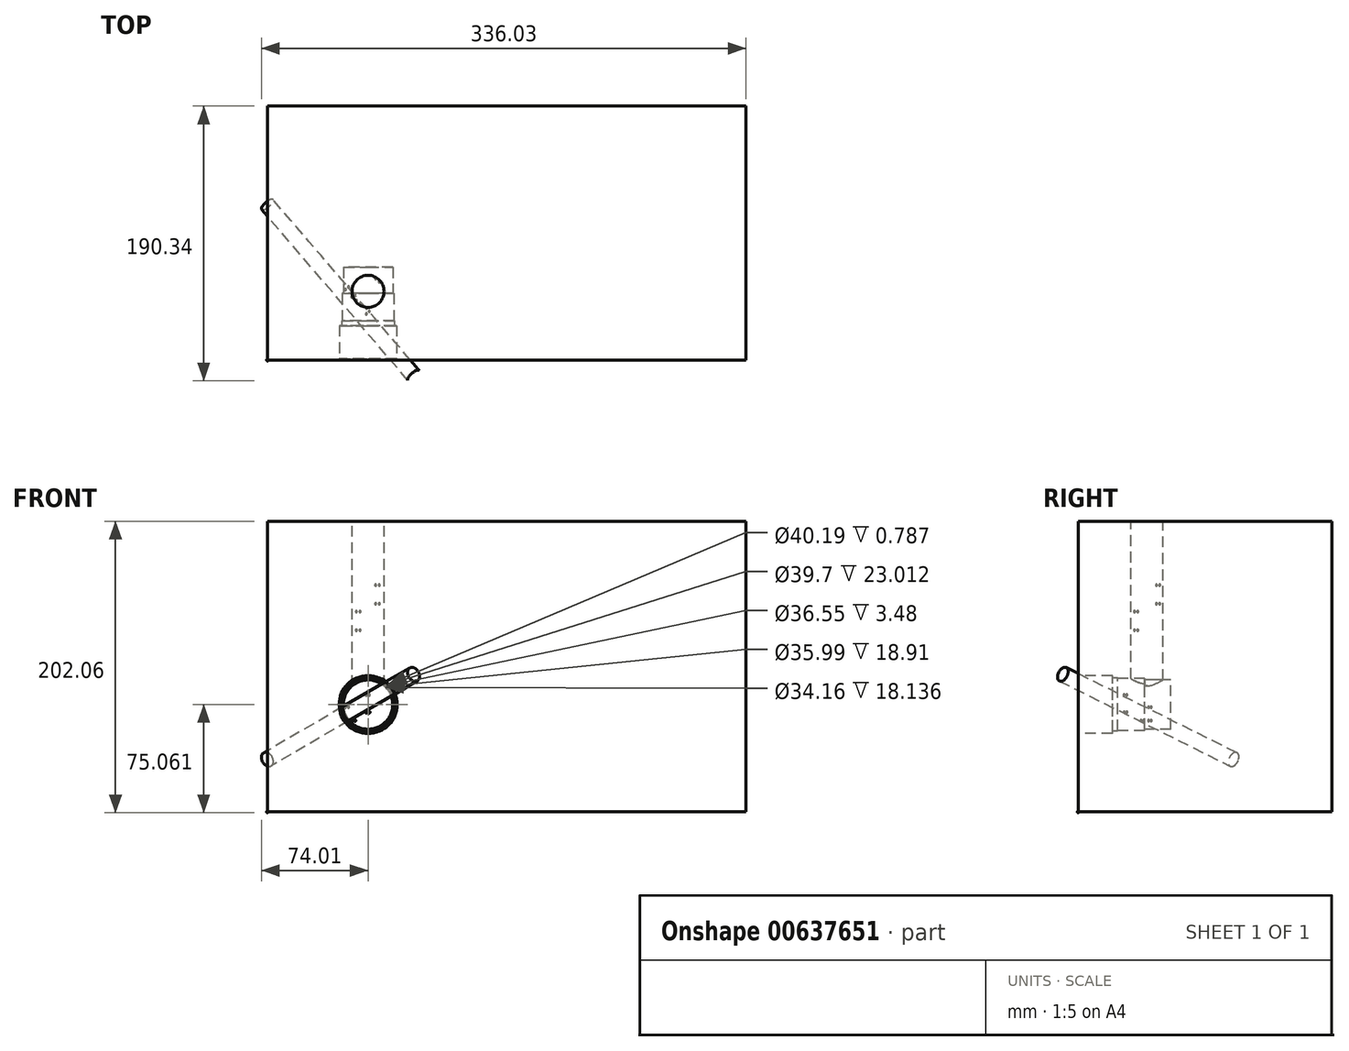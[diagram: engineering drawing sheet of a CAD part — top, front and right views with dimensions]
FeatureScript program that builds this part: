
annotation { "Feature Type Name" : "Feature", "Feature Type Description" : "" }
export const myFeature = defineFeature(function(context is Context, id is Id, definition is map)
    precondition{}
    {
        {
            var Q0;
            Q0=qCreatedBy(makeId("Top.planeOp"),FACE);
            var sketch = newSketch(context, id + "F0", { "sketchPlane" : qUnion([Q0])});
            skLineSegment(sketch, "E0.bottom", {"start": v(0, 0) * mm, "end": v(331.87, 0) * mm});
            skLineSegment(sketch, "E0.top", {"start": v(0, 176.02) * mm, "end": v(331.87, 176.02) * mm});
            skLineSegment(sketch, "E0.left", {"start": v(0, 0) * mm, "end": v(0, 176.02) * mm});
            skLineSegment(sketch, "E0.right", {"start": v(331.87, 0) * mm, "end": v(331.87, 176.02) * mm});
            skSolve(sketch);
        }
        {
            var Q0;
            Q0 = qSketchRegion(id + "F0", true);
            var Q1;
            Q1=sQuery(id+"F0.wireOp",EDGE,"E0.left");
            var Q2;
            Q2=sQuery(id+"F0.wireOp",EDGE,"E0.bottom");
            var Q3;
            Q3=sQuery(id+"F0.wireOp",EDGE,"E0.top");
            var Q4;
            Q4=sQuery(id+"F0.wireOp",EDGE,"E0.right");
            extrude(context, id + "F1", {"entities" : qUnion([Q0]), "surfaceEntities" : qUnion([Q1, Q2, Q3, Q4]), "depth" : 201.42 * mm, "offsetDistance" : 25.4 * mm});
        }
        {
            var Q0;
            Q0=qCreatedBy(makeId("Front.planeOp"),FACE);
            var sketch = newSketch(context, id + "F2", { "sketchPlane" : qUnion([Q0])});
            skArc(sketch, "E1", {"start": v(0, -0.64) * mm, "mid": v(0.64, 0) * mm, "end": v(0, 0.64) * mm});
            skLineSegment(sketch, "E2", {"start": v(0, 0.64) * mm, "end": v(0, -0.64) * mm});
            skSolve(sketch);
        }
        {
            var Q0;
            Q0=makeQuery(id+"F2.imprint","IMPRINT",FACE,{"disambiguationData":[TD([[makeQuery(id+"F2.imprint","IMPRINT",EDGE,{"derivedFrom":sQuery(id+"F2.wireOp",EDGE,"E1")}),1.0]])]});
            var Q1;
            Q1=sQuery(id+"F2.wireOp",EDGE,"E1");
            var Q2;
            Q2=sQuery(id+"F2.wireOp",EDGE,"E2");
            revolve(context, id + "F3", {"entities" : qUnion([Q0]), "surfaceEntities" : qUnion([Q1]), "axis" : qUnion([Q2]), "revolveType" : RevolveType.FULL});
        }
        {
            var Q0;
            Q0=makeQuery(id+"F3.opRevolve","SWEPT_BODY",BODY,{"disambiguationData":[OSD([sQuery(id+"F2.wireOp",EDGE,"E1"),sQuery(id+"F2.wireOp",EDGE,"E2")])]});
            transform(context, id + "F4", {"entities" : qUnion([Q0]), "transformType" : TransformType.TRANSLATION_3D, "dx" : 77.65 * mm, "dy" : 54.25 * mm, "dz" : 157.2 * mm, "makeCopy" : true});
        }
        {
            var Q0;
            Q0=makeQuery(id+"F3.opRevolve","SWEPT_BODY",BODY,{"disambiguationData":[OSD([sQuery(id+"F2.wireOp",EDGE,"E1"),sQuery(id+"F2.wireOp",EDGE,"E2")])]});
            transform(context, id + "F5", {"entities" : qUnion([Q0]), "transformType" : TransformType.TRANSLATION_3D, "dx" : 64.3 * mm, "dy" : 39.03 * mm, "dz" : 125.97 * mm, "makeCopy" : true});
        }
        {
            var Q0;
            Q0=makeQuery(id+"F3.opRevolve","SWEPT_BODY",BODY,{"disambiguationData":[OSD([sQuery(id+"F2.wireOp",EDGE,"E1"),sQuery(id+"F2.wireOp",EDGE,"E2")])]});
            transform(context, id + "F6", {"entities" : qUnion([Q0]), "transformType" : TransformType.TRANSLATION_3D, "dx" : 77.65 * mm, "dy" : 54.25 * mm, "dz" : 144.3 * mm, "makeCopy" : true});
        }
        {
            var Q0;
            Q0=makeQuery(id+"F3.opRevolve","SWEPT_BODY",BODY,{"disambiguationData":[OSD([sQuery(id+"F2.wireOp",EDGE,"E1"),sQuery(id+"F2.wireOp",EDGE,"E2")])]});
            transform(context, id + "F7", {"entities" : qUnion([Q0]), "transformType" : TransformType.TRANSLATION_3D, "dx" : 64.3 * mm, "dy" : 39.03 * mm, "dz" : 138.86 * mm, "makeCopy" : true});
        }
        {
            var Q0;
            Q0=makeQuery(id+"F3.opRevolve","SWEPT_BODY",BODY,{"disambiguationData":[OSD([sQuery(id+"F2.wireOp",EDGE,"E1"),sQuery(id+"F2.wireOp",EDGE,"E2")])]});
            transform(context, id + "F8", {"entities" : qUnion([Q0]), "transformType" : TransformType.TRANSLATION_3D, "dx" : 75.06 * mm, "dy" : 56.52 * mm, "dz" : 157.2 * mm, "makeCopy" : true});
        }
        {
            var Q0;
            Q0=makeQuery(id+"F3.opRevolve","SWEPT_BODY",BODY,{"disambiguationData":[OSD([sQuery(id+"F2.wireOp",EDGE,"E1"),sQuery(id+"F2.wireOp",EDGE,"E2")])]});
            transform(context, id + "F9", {"entities" : qUnion([Q0]), "transformType" : TransformType.TRANSLATION_3D, "dx" : 61.7 * mm, "dy" : 41.3 * mm, "dz" : 125.97 * mm, "makeCopy" : true});
        }
        {
            var Q0;
            Q0=makeQuery(id+"F3.opRevolve","SWEPT_BODY",BODY,{"disambiguationData":[OSD([sQuery(id+"F2.wireOp",EDGE,"E1"),sQuery(id+"F2.wireOp",EDGE,"E2")])]});
            transform(context, id + "F10", {"entities" : qUnion([Q0]), "transformType" : TransformType.TRANSLATION_3D, "dx" : 75.06 * mm, "dy" : 56.52 * mm, "dz" : 144.3 * mm, "makeCopy" : true});
        }
        {
            var Q0;
            Q0=makeQuery(id+"F3.opRevolve","SWEPT_BODY",BODY,{"disambiguationData":[OSD([sQuery(id+"F2.wireOp",EDGE,"E1"),sQuery(id+"F2.wireOp",EDGE,"E2")])]});
            transform(context, id + "F11", {"entities" : qUnion([Q0]), "transformType" : TransformType.TRANSLATION_3D, "dx" : 61.7 * mm, "dy" : 41.3 * mm, "dz" : 138.86 * mm, "makeCopy" : true});
        }
        {
            var Q0;
            Q0=makeQuery(id+"F1.opExtrude","CAP_FACE",FACE,{"disambiguationData":[OSD([sQuery(id+"F0.wireOp",EDGE,"E0.bottom"),sQuery(id+"F0.wireOp",EDGE,"E0.top"),sQuery(id+"F0.wireOp",EDGE,"E0.left"),sQuery(id+"F0.wireOp",EDGE,"E0.right")])],"isStart":false});
            var sketch = newSketch(context, id + "F12", { "sketchPlane" : qUnion([Q0])});
            skCircle(sketch, "E3", {"center": v(69.85, 47.62) * mm, "radius": 11.11 * mm});
            skSolve(sketch);
        }
        {
            var Q0;
            Q0 = qSketchRegion(id + "F12", true);
            var Q1;
            Q1=makeQuery(id+"F1.opExtrude","CAP_FACE",FACE,{"disambiguationData":[OSD([sQuery(id+"F0.wireOp",EDGE,"E0.bottom"),sQuery(id+"F0.wireOp",EDGE,"E0.top"),sQuery(id+"F0.wireOp",EDGE,"E0.left"),sQuery(id+"F0.wireOp",EDGE,"E0.right")])],"isStart":false});
            extrude(context, id + "F13", {"entities" : qUnion([Q0]), "oppositeDirection" : true, "depth" : 138.11 * mm, "endBoundEntityFace" : qUnion([Q1]), "offsetDistance" : 25.4 * mm});
        }
        {
            var Q0;
            Q0=makeQuery(id+"F1.opExtrude","SWEPT_FACE",FACE,{"disambiguationData":[OSD([sQuery(id+"F0.wireOp",EDGE,"E0.bottom")])]});
            var sketch = newSketch(context, id + "F14", { "sketchPlane" : qUnion([Q0])});
            skCircle(sketch, "E4", {"center": v(69.85, 74.42) * mm, "radius": 20.1 * mm});
            skSolve(sketch);
        }
        {
            var Q0;
            Q0 = qSketchRegion(id + "F14", true);
            extrude(context, id + "F15", {"entities" : qUnion([Q0]), "operationType" : NewBodyOperationType.REMOVE, "oppositeDirection" : true, "depth" : 0.79 * mm, "offsetDistance" : 25.4 * mm});
        }
        {
            var Q0;
            Q0=makeQuery(id+"F15.boolean.opBoolean","COPY",FACE,{"derivedFrom":makeQuery(id+"F15.opExtrude","CAP_FACE",FACE,{"disambiguationData":[OSD([sQuery(id+"F14.wireOp",EDGE,"E4")])],"isStart":false})});
            var sketch = newSketch(context, id + "F16", { "sketchPlane" : qUnion([Q0])});
            skCircle(sketch, "E5", {"center": v(69.85, 74.42) * mm, "radius": 19.85 * mm});
            skSolve(sketch);
        }
        {
            var Q0;
            Q0 = qSketchRegion(id + "F16", true);
            extrude(context, id + "F17", {"entities" : qUnion([Q0]), "operationType" : NewBodyOperationType.REMOVE, "oppositeDirection" : true, "depth" : 21.44 * mm, "offsetDistance" : 25.4 * mm});
        }
        {
            var Q0;
            Q0=makeQuery(id+"F17.boolean.opBoolean","COPY",FACE,{"derivedFrom":makeQuery(id+"F17.opExtrude","CAP_FACE",FACE,{"disambiguationData":[OSD([sQuery(id+"F16.wireOp",EDGE,"E5")])],"isStart":false})});
            var sketch = newSketch(context, id + "F18", { "sketchPlane" : qUnion([Q0])});
            skCircle(sketch, "E6", {"center": v(69.85, 74.42) * mm, "radius": 19.85 * mm});
            skSolve(sketch);
        }
        {
            var Q0;
            Q0 = qSketchRegion(id + "F18", true);
            extrude(context, id + "F19", {"entities" : qUnion([Q0]), "operationType" : NewBodyOperationType.REMOVE, "oppositeDirection" : true, "depth" : 1.57 * mm, "offsetDistance" : 25.4 * mm});
        }
        {
            var Q0;
            Q0=makeQuery(id+"F19.boolean.opBoolean","COPY",FACE,{"derivedFrom":makeQuery(id+"F19.opExtrude","CAP_FACE",FACE,{"disambiguationData":[OSD([sQuery(id+"F18.wireOp",EDGE,"E6")])],"isStart":false})});
            var sketch = newSketch(context, id + "F20", { "sketchPlane" : qUnion([Q0])});
            skCircle(sketch, "E7", {"center": v(69.85, 74.42) * mm, "radius": 18.28 * mm});
            skSolve(sketch);
        }
        {
            var Q0;
            Q0 = qSketchRegion(id + "F20", true);
            extrude(context, id + "F21", {"entities" : qUnion([Q0]), "operationType" : NewBodyOperationType.REMOVE, "oppositeDirection" : true, "depth" : 3.2 * mm, "offsetDistance" : 25.4 * mm});
        }
        {
            var Q0;
            Q0=makeQuery(id+"F21.boolean.opBoolean","COPY",FACE,{"derivedFrom":makeQuery(id+"F21.opExtrude","CAP_FACE",FACE,{"disambiguationData":[OSD([sQuery(id+"F20.wireOp",EDGE,"E7")])],"isStart":false})});
            var sketch = newSketch(context, id + "F22", { "sketchPlane" : qUnion([Q0])});
            skCircle(sketch, "E8", {"center": v(69.85, 74.42) * mm, "radius": 18.28 * mm});
            skSolve(sketch);
        }
        {
            var Q0;
            Q0 = qSketchRegion(id + "F22", true);
            extrude(context, id + "F23", {"entities" : qUnion([Q0]), "operationType" : NewBodyOperationType.REMOVE, "oppositeDirection" : true, "depth" : 0.28 * mm, "offsetDistance" : 25.4 * mm});
        }
        {
            var Q0;
            Q0=makeQuery(id+"F23.boolean.opBoolean","COPY",FACE,{"derivedFrom":makeQuery(id+"F23.opExtrude","CAP_FACE",FACE,{"disambiguationData":[OSD([sQuery(id+"F22.wireOp",EDGE,"E8")])],"isStart":false})});
            var sketch = newSketch(context, id + "F24", { "sketchPlane" : qUnion([Q0])});
            skCircle(sketch, "E9", {"center": v(69.85, 74.42) * mm, "radius": 18 * mm});
            skSolve(sketch);
        }
        {
            var Q0;
            Q0 = qSketchRegion(id + "F24", true);
            extrude(context, id + "F25", {"entities" : qUnion([Q0]), "operationType" : NewBodyOperationType.REMOVE, "oppositeDirection" : true, "depth" : 18 * mm, "offsetDistance" : 25.4 * mm});
        }
        {
            var Q0;
            Q0=makeQuery(id+"F25.boolean.opBoolean","COPY",FACE,{"derivedFrom":makeQuery(id+"F25.opExtrude","CAP_FACE",FACE,{"disambiguationData":[OSD([sQuery(id+"F24.wireOp",EDGE,"E9")])],"isStart":false})});
            var sketch = newSketch(context, id + "F26", { "sketchPlane" : qUnion([Q0])});
            skCircle(sketch, "E10", {"center": v(69.85, 74.42) * mm, "radius": 18 * mm});
            skSolve(sketch);
        }
        {
            var Q0;
            Q0 = qSketchRegion(id + "F26", true);
            extrude(context, id + "F27", {"entities" : qUnion([Q0]), "operationType" : NewBodyOperationType.REMOVE, "oppositeDirection" : true, "depth" : 0.91 * mm, "offsetDistance" : 25.4 * mm});
        }
        {
            var Q0;
            Q0=makeQuery(id+"F27.boolean.opBoolean","COPY",FACE,{"derivedFrom":makeQuery(id+"F27.opExtrude","CAP_FACE",FACE,{"disambiguationData":[OSD([sQuery(id+"F26.wireOp",EDGE,"E10")])],"isStart":false})});
            var sketch = newSketch(context, id + "F28", { "sketchPlane" : qUnion([Q0])});
            skCircle(sketch, "E11", {"center": v(69.85, 74.42) * mm, "radius": 17.08 * mm});
            skSolve(sketch);
        }
        {
            var Q0;
            Q0 = qSketchRegion(id + "F28", true);
            extrude(context, id + "F29", {"entities" : qUnion([Q0]), "operationType" : NewBodyOperationType.REMOVE, "oppositeDirection" : true, "depth" : 18.14 * mm, "offsetDistance" : 25.4 * mm});
        }
        {
            var Q0;
            Q0=makeQuery(id+"F1.opExtrude","SWEPT_FACE",FACE,{"disambiguationData":[OSD([sQuery(id+"F0.wireOp",EDGE,"E0.left")])]});
            var sketch = newSketch(context, id + "F30", { "sketchPlane" : qUnion([Q0])});
            skPoint(sketch, "E12", {"position": v(-107.8, 36.4) * mm});
            skSolve(sketch);
        }
        {
            var Q0;
            Q0=qCreatedBy(makeId("Top.planeOp"),FACE);
            cPlane(context, id + "F31", {"entities" : qUnion([Q0]), "cplaneType" : CPlaneType.OFFSET, "offset" : 90.1 * mm, "width" : 152.4 * mm, "height" : 152.4 * mm});
        }
        {
            var Q0;
            Q0=qCreatedBy(id+"F31.planeOp",FACE);
            var sketch = newSketch(context, id + "F32", { "sketchPlane" : qUnion([Q0])});
            skPoint(sketch, "E13", {"position": v(92.28, 0) * mm});
            skSolve(sketch);
        }
        {
            var Q0;
            {var subQ0=sQuery(id+"F0.wireOp",EDGE,"E0.left");Q0=makeQuery(id+"F30.imprint","IMPRINT",FACE,{"disambiguationData":[TD([[makeQuery(id+"F30.imprint","IMPRINT",EDGE,{"derivedFrom":makeQuery(id+"F1.opExtrude","CAP_EDGE",EDGE,{"disambiguationData":[OSD([subQ0])],"isStart":true})}),-1.0]])]});}
            var sketch = newSketch(context, id + "F33", { "sketchPlane" : qUnion([Q0])});
            skPoint(sketch, "E14", {"position": v(0, 90.1) * mm});
            skSolve(sketch);
        }
        {
            var Q0;
            Q0=sQuery(id+"F30.wireOp",VERTEX,"E12");
            var Q1;
            Q1=sQuery(id+"F33.wireOp",VERTEX,"E14");
            var Q2;
            Q2=sQuery(id+"F32.wireOp",VERTEX,"E13");
            cPlane(context, id + "F34", {"entities" : qUnion([Q0, Q1, Q2]), "cplaneType" : CPlaneType.THREE_POINT, "offset" : 25.4 * mm, "width" : 152.4 * mm, "height" : 152.4 * mm});
        }
        {
            var Q0;
            Q0=qCreatedBy(id+"F34.planeOp",FACE);
            var sketch = newSketch(context, id + "F35", { "sketchPlane" : qUnion([Q0])});
            skLineSegment(sketch, "E15", {"start": v(0, -80.27) * mm, "end": v(92.28, 40.18) * mm, "construction": true});
            skSolve(sketch);
        }
        {
            var Q0;
            Q0=sQuery(id+"F30.wireOp",VERTEX,"E12");
            var Q1;
            Q1=sQuery(id+"F35.wireOp",EDGE,"E15");
            cPlane(context, id + "F36", {"entities" : qUnion([Q0, Q1]), "cplaneType" : CPlaneType.LINE_POINT, "offset" : 25.4 * mm, "width" : 152.4 * mm, "height" : 152.4 * mm});
        }
        {
            var Q0;
            Q0=qCreatedBy(id+"F36.planeOp",FACE);
            var sketch = newSketch(context, id + "F37", { "sketchPlane" : qUnion([Q0])});
            skCircle(sketch, "E16", {"center": v(48.82, 80.65) * mm, "radius": 5.25 * mm});
            skSolve(sketch);
        }
        {
            var Q0;
            Q0 = qSketchRegion(id + "F37", true);
            extrude(context, id + "F38", {"entities" : qUnion([Q0]), "depth" : 166.7 * mm, "offsetDistance" : 25.4 * mm});
        }
        {
            var Q0;
            Q0=makeQuery(id+"F3.opRevolve","SWEPT_BODY",BODY,{"disambiguationData":[OSD([sQuery(id+"F2.wireOp",EDGE,"E1"),sQuery(id+"F2.wireOp",EDGE,"E2")])]});
            transform(context, id + "F39", {"entities" : qUnion([Q0]), "transformType" : TransformType.TRANSLATION_3D, "dx" : 70.72 * mm, "dy" : 33.74 * mm, "dz" : 69.14 * mm, "makeCopy" : true});
        }
        {
            var Q0;
            Q0=makeQuery(id+"F3.opRevolve","SWEPT_BODY",BODY,{"disambiguationData":[OSD([sQuery(id+"F2.wireOp",EDGE,"E1"),sQuery(id+"F2.wireOp",EDGE,"E2")])]});
            transform(context, id + "F40", {"entities" : qUnion([Q0]), "transformType" : TransformType.TRANSLATION_3D, "dx" : 68.63 * mm, "dy" : 31.96 * mm, "dz" : 69.14 * mm, "makeCopy" : true});
        }
        {
            var Q0;
            Q0=makeQuery(id+"F3.opRevolve","SWEPT_BODY",BODY,{"disambiguationData":[OSD([sQuery(id+"F2.wireOp",EDGE,"E1"),sQuery(id+"F2.wireOp",EDGE,"E2")])]});
            transform(context, id + "F41", {"entities" : qUnion([Q0]), "transformType" : TransformType.TRANSLATION_3D, "dx" : 60.7 * mm, "dy" : 45.46 * mm, "dz" : 63.3 * mm, "makeCopy" : true});
        }
        {
            var Q0;
            Q0=makeQuery(id+"F3.opRevolve","SWEPT_BODY",BODY,{"disambiguationData":[OSD([sQuery(id+"F2.wireOp",EDGE,"E1"),sQuery(id+"F2.wireOp",EDGE,"E2")])]});
            transform(context, id + "F42", {"entities" : qUnion([Q0]), "transformType" : TransformType.TRANSLATION_3D, "dx" : 58.6 * mm, "dy" : 43.67 * mm, "dz" : 63.3 * mm, "makeCopy" : true});
        }
        {
            var Q0;
            Q0=makeQuery(id+"F3.opRevolve","SWEPT_BODY",BODY,{"disambiguationData":[OSD([sQuery(id+"F2.wireOp",EDGE,"E1"),sQuery(id+"F2.wireOp",EDGE,"E2")])]});
            transform(context, id + "F43", {"entities" : qUnion([Q0]), "transformType" : TransformType.TRANSLATION_3D, "dx" : 70.72 * mm, "dy" : 33.74 * mm, "dz" : 81.04 * mm, "makeCopy" : true});
        }
        {
            var Q0;
            Q0=makeQuery(id+"F3.opRevolve","SWEPT_BODY",BODY,{"disambiguationData":[OSD([sQuery(id+"F2.wireOp",EDGE,"E1"),sQuery(id+"F2.wireOp",EDGE,"E2")])]});
            transform(context, id + "F44", {"entities" : qUnion([Q0]), "transformType" : TransformType.TRANSLATION_3D, "dx" : 68.63 * mm, "dy" : 31.96 * mm, "dz" : 81.04 * mm, "makeCopy" : true});
        }
        {
            var Q0;
            Q0=makeQuery(id+"F3.opRevolve","SWEPT_BODY",BODY,{"disambiguationData":[OSD([sQuery(id+"F2.wireOp",EDGE,"E1"),sQuery(id+"F2.wireOp",EDGE,"E2")])]});
            transform(context, id + "F45", {"entities" : qUnion([Q0]), "transformType" : TransformType.TRANSLATION_3D, "dx" : 56.27 * mm, "dy" : 50.63 * mm, "dz" : 72.63 * mm, "makeCopy" : true});
        }
        {
            var Q0;
            Q0=makeQuery(id+"F3.opRevolve","SWEPT_BODY",BODY,{"disambiguationData":[OSD([sQuery(id+"F2.wireOp",EDGE,"E1"),sQuery(id+"F2.wireOp",EDGE,"E2")])]});
            transform(context, id + "F46", {"entities" : qUnion([Q0]), "transformType" : TransformType.TRANSLATION_3D, "dx" : 54.18 * mm, "dy" : 48.84 * mm, "dz" : 72.63 * mm, "makeCopy" : true});
        }
        {
            var Q0;
            Q0=makeQuery(id+"F3.opRevolve","SWEPT_BODY",BODY,{"disambiguationData":[OSD([sQuery(id+"F2.wireOp",EDGE,"E1"),sQuery(id+"F2.wireOp",EDGE,"E2")])]});
            transform(context, id + "F47", {"entities" : qUnion([Q0]), "transformType" : TransformType.TRANSLATION_3D, "dx" : 56.27 * mm, "dy" : 50.63 * mm, "dz" : 63.3 * mm, "makeCopy" : true});
        }
        {
            var Q0;
            Q0=makeQuery(id+"F3.opRevolve","SWEPT_BODY",BODY,{"disambiguationData":[OSD([sQuery(id+"F2.wireOp",EDGE,"E1"),sQuery(id+"F2.wireOp",EDGE,"E2")])]});
            transform(context, id + "F48", {"entities" : qUnion([Q0]), "transformType" : TransformType.TRANSLATION_3D, "dx" : 54.18 * mm, "dy" : 48.84 * mm, "dz" : 63.3 * mm, "makeCopy" : true});
        }
    });
